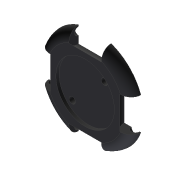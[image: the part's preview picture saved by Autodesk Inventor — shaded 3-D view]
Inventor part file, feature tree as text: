
AUTODESK INVENTOR PART (.ipt)
format: ipt  version: 2017 (Build 210142000, 142)  size: 176,640 bytes
history: native  units: mm
features: sketch x5, extrude x3, revolve x1, fillet x1, pattern_circular x1, hole x1, projected_geometry x1
ambient origin geometry x8: Origin, YZ Plane, XZ Plane, XY Plane, X Axis, Y Axis, Z Axis, Center Point
bodies: Solid1 (feature_tree)
feature tree (13):
  extrude  "Extrusion1"  Depth=6.0mm TaperAngle=0.0deg
  revolve  "Revolution1"  [1 undecoded]
  extrude  "Extrusion2"  Depth=5.0mm
  fillet  "Fillet1"  Radius=5.0mm
  pattern_circular  "Circular Pattern1"  [2 undecoded]
  extrude  "Extrusion3"  Depth=2.0mm TaperAngle=360.0deg
  hole  "Hole1"  [1 undecoded]
  sketch  "Sketch1"  dims[d0=60.0mm d1=6.0mm d2=0.0mm]
  sketch  "Sketch2"  dims[d3=20.0mm d4=25.0mm]
  sketch  "Sketch3"  dims[d5=14.0mm d6=5.0mm d7=5.0mm]
  projected_geometry  "Projected Loop1"
  sketch  "Sketch4"  dims[d8=90.0deg]
  sketch  "Sketch5"  dims[d9=6.0mm d10=0.0mm d11=6.0mm d12=40.0mm d13=360.0deg d15=36.0mm d16=2.0mm d17=0.0mm d19=45.0deg d20=14.0mm d21=14.0mm d22=180.0deg d23=4.0mm d24=6.0mm d25=4.0mm d26=2.0mm d27=90.0deg d28=8.0mm d29=20.594885mm]
note: 4 required parameter values undecoded (feature->parameter linkage not recoverable at this tier; creation-order binding heuristic only, values carry confidence <= 0.55)